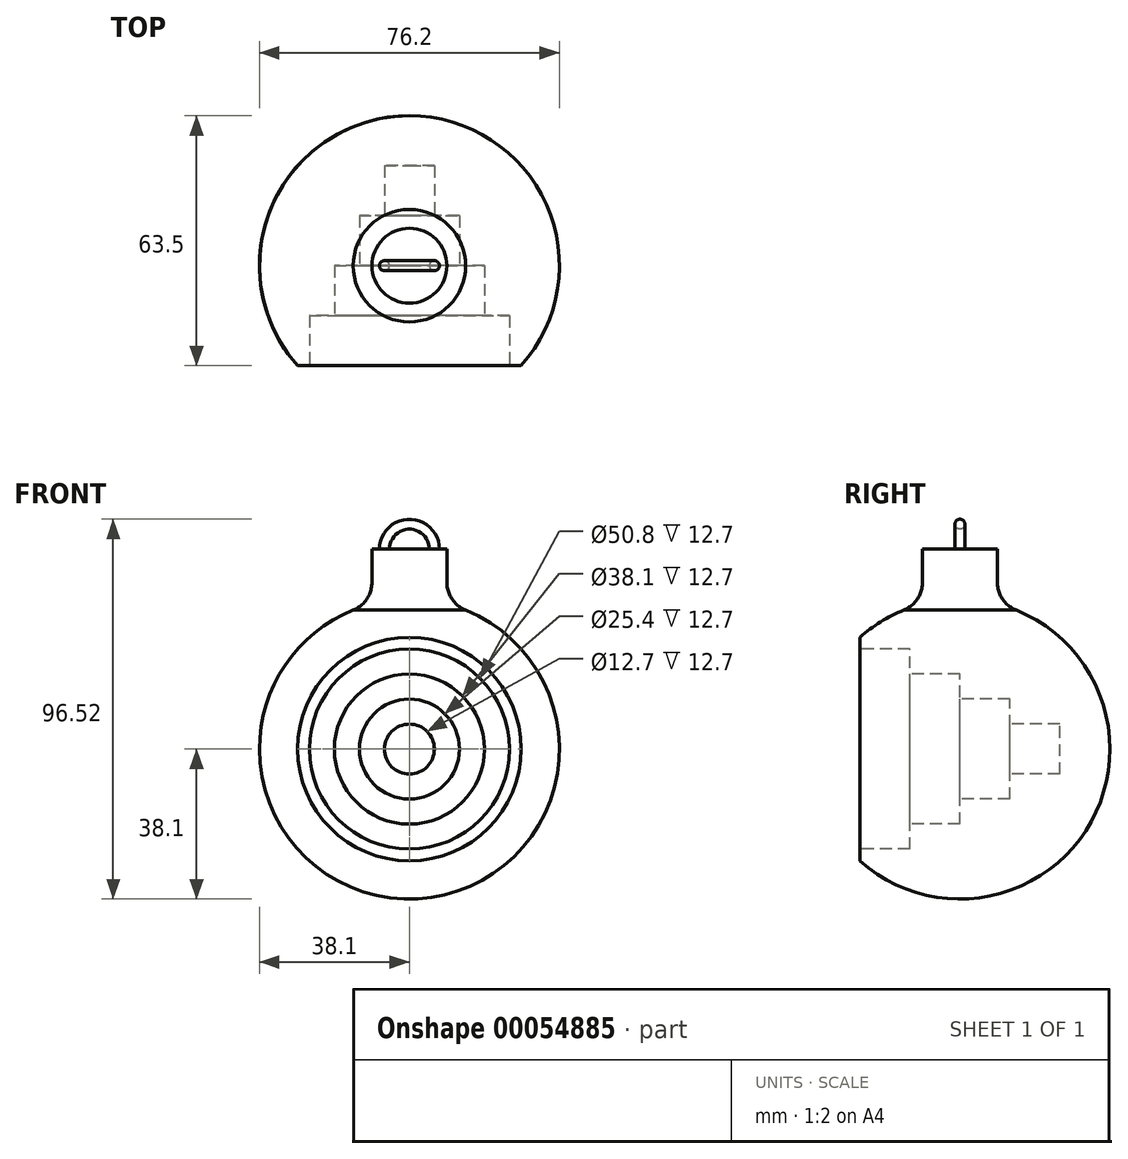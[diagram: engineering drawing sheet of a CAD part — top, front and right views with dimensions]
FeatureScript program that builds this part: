
annotation { "Feature Type Name" : "Feature", "Feature Type Description" : "" }
export const myFeature = defineFeature(function(context is Context, id is Id, definition is map)
    precondition{}
    {
        {
            var Q0;
            Q0=qCreatedBy(makeId("Top.planeOp"),FACE);
            var sketch = newSketch(context, id + "F0", { "sketchPlane" : qUnion([Q0])});
            skCircle(sketch, "E0", {"center": v(0, 0) * mm, "radius": 38.1 * mm});
            skLineSegment(sketch, "E1", {"start": v(0, -38.1) * mm, "end": v(0, 38.1) * mm});
            skSolve(sketch);
        }
        {
            var Q0;
            {var subQ0=sQuery(id+"F0.wireOp",EDGE,"E1");Q0=makeQuery(id+"F0.imprint","IMPRINT",FACE,{"disambiguationData":[TD([[makeQuery(id+"F0.imprint","IMPRINT",EDGE,{"derivedFrom":subQ0}),-1.0]])]});}
            var Q1;
            Q1=sQuery(id+"F0.wireOp",EDGE,"E1");
            revolve(context, id + "F1", {"entities" : qUnion([Q0]), "axis" : qUnion([Q1]), "revolveType" : RevolveType.FULL});
        }
        {
            var Q0;
            Q0=qCreatedBy(makeId("Front.planeOp"),FACE);
            cPlane(context, id + "F2", {"entities" : qUnion([Q0]), "cplaneType" : CPlaneType.OFFSET, "offset" : 38.1 * mm, "width" : 152.4 * mm, "height" : 152.4 * mm});
        }
        {
            var Q0;
            Q0=qCreatedBy(id+"F2.planeOp",FACE);
            var sketch = newSketch(context, id + "F3", { "sketchPlane" : qUnion([Q0])});
            skCircle(sketch, "E2", {"center": v(0, 0) * mm, "radius": 38.1 * mm});
            skCircle(sketch, "E3", {"center": v(0, 0) * mm, "radius": 12.7 * mm});
            skCircle(sketch, "E4", {"center": v(0, 0) * mm, "radius": 19.05 * mm});
            skCircle(sketch, "E5", {"center": v(0, 0) * mm, "radius": 25.4 * mm});
            skCircle(sketch, "E6", {"center": v(0, 0) * mm, "radius": 6.35 * mm});
            skCircle(sketch, "E7", {"center": v(0, 0) * mm, "radius": 31.75 * mm});
            skSolve(sketch);
        }
        {
            var Q0;
            Q0=makeQuery(id+"F3.imprint","IMPRINT",FACE,{"disambiguationData":[TD([[makeQuery(id+"F3.imprint","IMPRINT",EDGE,{"derivedFrom":sQuery(id+"F3.wireOp",EDGE,"E6")}),1.0]])]});
            extrude(context, id + "F4", {"entities" : qUnion([Q0]), "operationType" : NewBodyOperationType.REMOVE, "oppositeDirection" : true, "depth" : 63.5 * mm});
        }
        {
            var Q0;
            Q0=makeQuery(id+"F3.imprint","IMPRINT",FACE,{"disambiguationData":[TD([[makeQuery(id+"F3.imprint","IMPRINT",EDGE,{"derivedFrom":sQuery(id+"F3.wireOp",EDGE,"E3")}),1.0]])]});
            extrude(context, id + "F5", {"entities" : qUnion([Q0]), "operationType" : NewBodyOperationType.REMOVE, "oppositeDirection" : true, "depth" : 50.8 * mm});
        }
        {
            var Q0;
            Q0=makeQuery(id+"F3.imprint","IMPRINT",FACE,{"disambiguationData":[TD([[makeQuery(id+"F3.imprint","IMPRINT",EDGE,{"derivedFrom":sQuery(id+"F3.wireOp",EDGE,"E3")}),-1.0]])]});
            extrude(context, id + "F6", {"entities" : qUnion([Q0]), "operationType" : NewBodyOperationType.REMOVE, "oppositeDirection" : true, "depth" : 38.1 * mm});
        }
        {
            var Q0;
            Q0=makeQuery(id+"F3.imprint","IMPRINT",FACE,{"disambiguationData":[TD([[makeQuery(id+"F3.imprint","IMPRINT",EDGE,{"derivedFrom":sQuery(id+"F3.wireOp",EDGE,"E4")}),-1.0]])]});
            extrude(context, id + "F7", {"entities" : qUnion([Q0]), "operationType" : NewBodyOperationType.REMOVE, "oppositeDirection" : true, "depth" : 25.4 * mm});
        }
        {
            var Q0;
            Q0=makeQuery(id+"F3.imprint","IMPRINT",FACE,{"disambiguationData":[TD([[makeQuery(id+"F3.imprint","IMPRINT",EDGE,{"derivedFrom":sQuery(id+"F3.wireOp",EDGE,"E5")}),-1.0]])]});
            extrude(context, id + "F8", {"entities" : qUnion([Q0]), "operationType" : NewBodyOperationType.REMOVE, "oppositeDirection" : true, "depth" : 12.7 * mm});
        }
        {
            var Q0;
            Q0=qCreatedBy(makeId("Top.planeOp"),FACE);
            cPlane(context, id + "F9", {"entities" : qUnion([Q0]), "cplaneType" : CPlaneType.OFFSET, "offset" : 38.1 * mm, "width" : 152.4 * mm, "height" : 152.4 * mm});
        }
        {
            var Q0;
            Q0=qCreatedBy(id+"F9.planeOp",FACE);
            var sketch = newSketch(context, id + "F10", { "sketchPlane" : qUnion([Q0])});
            skArc(sketch, "E8", {"start": v(28.4, -25.4) * mm, "mid": v(0, 38.1) * mm, "end": v(-28.4, -25.4) * mm});
            skCircle(sketch, "E9", {"center": v(0, 0) * mm, "radius": 9.53 * mm});
            skSolve(sketch);
        }
        {
            var Q0;
            Q0=makeQuery(id+"F10.imprint","IMPRINT",FACE,{"disambiguationData":[TD([[makeQuery(id+"F10.imprint","IMPRINT",EDGE,{"derivedFrom":sQuery(id+"F10.wireOp",EDGE,"E9")}),1.0]])]});
            extrude(context, id + "F11", {"entities" : qUnion([Q0]), "operationType" : NewBodyOperationType.ADD, "endBound" : BoundingType.SYMMETRIC, "depth" : 25.4 * mm});
        }
        {
            var Q0;
            Q0=makeQuery(id+"F11.boolean.opBoolean","INTERSECT",EDGE,{"derivedFrom":[makeQuery(id+"F1.opRevolve","SWEPT_FACE",FACE,{"disambiguationData":[OSD([sQuery(id+"F0.wireOp",EDGE,"E0")])]}),makeQuery(id+"F11.opExtrude","SWEPT_FACE",FACE,{"disambiguationData":[OSD([sQuery(id+"F10.wireOp",EDGE,"E9")])]})]});
            fillet(context, id + "F12", {"entities" : qUnion([Q0]), "radius" : 7.62 * mm, "tangentPropagation" : true, "allowEdgeOverflow" : false});
        }
        {
            var Q0;
            Q0=qCreatedBy(makeId("Front.planeOp"),FACE);
            var sketch = newSketch(context, id + "F13", { "sketchPlane" : qUnion([Q0])});
            skArc(sketch, "E10", {"start": v(9.52, 42.38) * mm, "mid": v(10.83, 38.12) * mm, "end": v(14.29, 35.32) * mm});
            skArc(sketch, "E11", {"start": v(-14.29, 35.32) * mm, "mid": v(-10.83, 38.12) * mm, "end": v(-9.52, 42.38) * mm});
            skLineSegment(sketch, "E12", {"start": v(-9.53, 42.38) * mm, "end": v(-9.53, 50.8) * mm});
            skLineSegment(sketch, "E13", {"start": v(9.53, 50.8) * mm, "end": v(9.53, 42.38) * mm});
            skLineSegment(sketch, "E14.0", {"start": v(-9.53, 50.8) * mm, "end": v(9.53, 50.8) * mm});
            skArc(sketch, "E15", {"start": v(6.35, 50.8) * mm, "mid": v(0, 57.15) * mm, "end": v(-6.35, 50.8) * mm});
            skSolve(sketch);
        }
        {
            var Q0;
            Q0=makeQuery(id+"F11.opExtrude","CAP_FACE",FACE,{"disambiguationData":[OSD([sQuery(id+"F10.wireOp",EDGE,"E9")])],"isStart":false});
            var sketch = newSketch(context, id + "F14", { "sketchPlane" : qUnion([Q0])});
            skLineSegment(sketch, "E16.0", {"start": v(6.35, 0) * mm, "end": v(-6.35, 0) * mm});
            skCircle(sketch, "E17", {"center": v(-6.35, 0) * mm, "radius": 1.27 * mm});
            skSolve(sketch);
        }
        {
            var Q0;
            Q0=makeQuery(id+"F14.imprint","IMPRINT",FACE,{"disambiguationData":[TD([[makeQuery(id+"F14.imprint","IMPRINT",EDGE,{"derivedFrom":sQuery(id+"F14.wireOp",EDGE,"E17")}),1.0]])]});
            var Q1;
            Q1=sQuery(id+"F13.wireOp",EDGE,"E15");
            sweep(context, id + "F15", {"operationType" : NewBodyOperationType.ADD, "profiles" : qUnion([Q0]), "path" : qUnion([Q1])});
        }
    });
